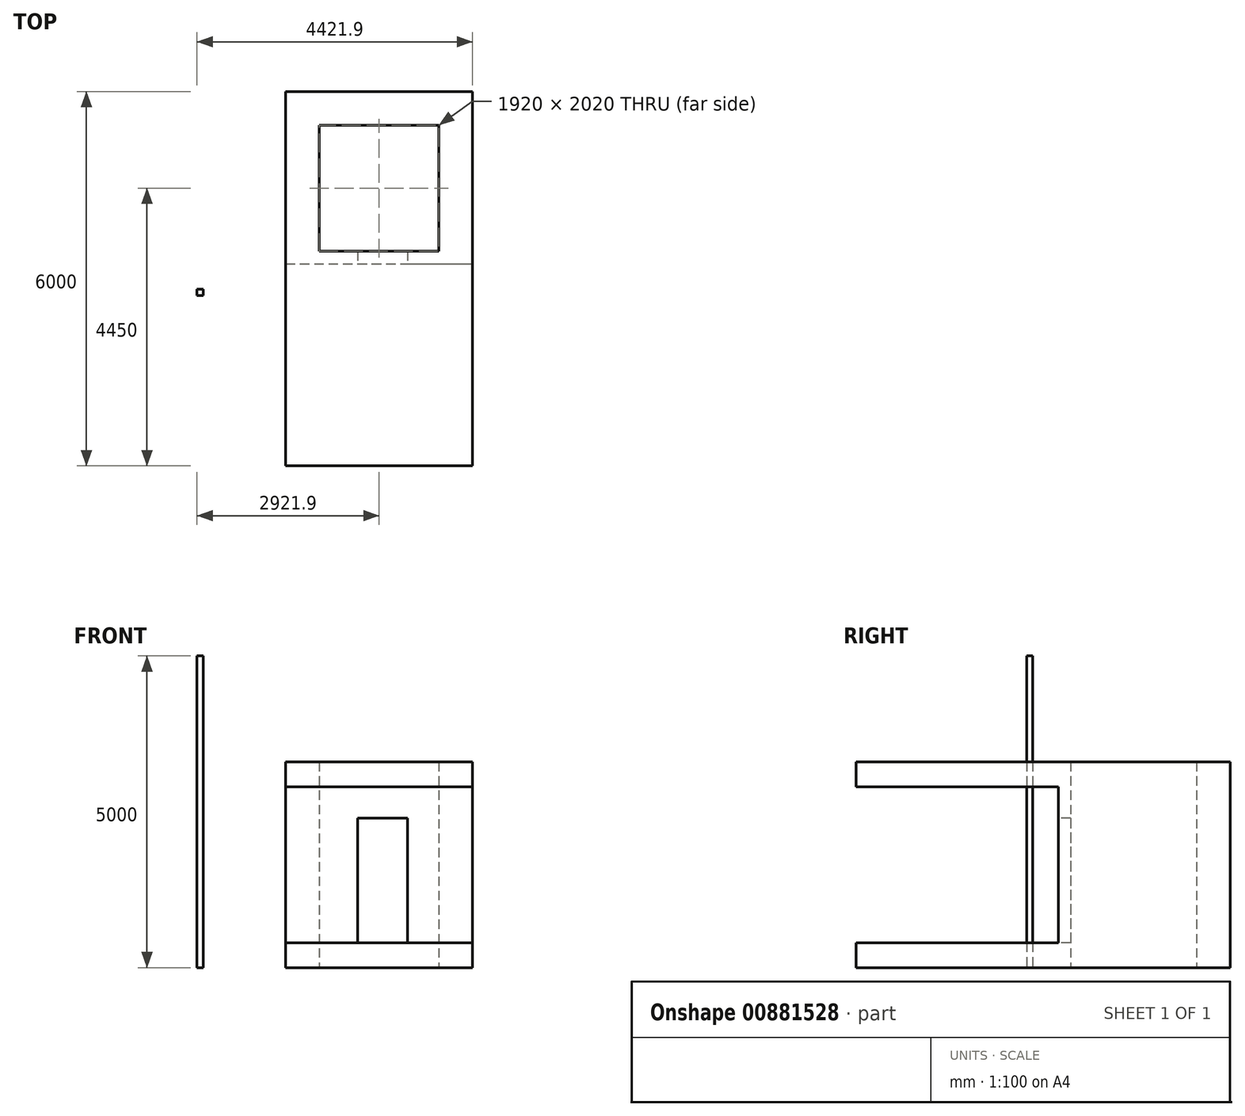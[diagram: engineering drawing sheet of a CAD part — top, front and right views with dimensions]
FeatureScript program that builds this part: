
annotation { "Feature Type Name" : "Feature", "Feature Type Description" : "" }
export const myFeature = defineFeature(function(context is Context, id is Id, definition is map)
    precondition{}
    {
        {
            var Q0;
            Q0=qCreatedBy(makeId("Top.planeOp"),FACE);
            var sketch = newSketch(context, id + "F0", { "sketchPlane" : qUnion([Q0])});
            skLineSegment(sketch, "E0.bottom", {"start": v(-1497.46, 4552.93) * mm, "end": v(1502.54, 4552.93) * mm});
            skLineSegment(sketch, "E0.top", {"start": v(-1497.46, -1447.07) * mm, "end": v(1502.54, -1447.07) * mm});
            skLineSegment(sketch, "E0.left", {"start": v(-1497.46, 4552.93) * mm, "end": v(-1497.46, -1447.07) * mm});
            skLineSegment(sketch, "E0.right", {"start": v(1502.54, 4552.93) * mm, "end": v(1502.54, -1447.07) * mm});
            skLineSegment(sketch, "E1.bottom", {"start": v(-957.46, 4012.93) * mm, "end": v(962.54, 4012.93) * mm});
            skLineSegment(sketch, "E1.top", {"start": v(-957.46, 1992.93) * mm, "end": v(962.54, 1992.93) * mm});
            skLineSegment(sketch, "E1.left", {"start": v(-957.46, 4012.93) * mm, "end": v(-957.46, 1992.93) * mm});
            skLineSegment(sketch, "E1.right", {"start": v(962.54, 4012.93) * mm, "end": v(962.54, 1992.93) * mm});
            skSolve(sketch);
        }
        {
            var Q0;
            Q0=makeQuery(id+"F0.imprint","IMPRINT",FACE,{"disambiguationData":[TD([[makeQuery(id+"F0.imprint","IMPRINT",EDGE,{"derivedFrom":sQuery(id+"F0.wireOp",EDGE,"E0.bottom")}),-1.0]])]});
            extrude(context, id + "F1", {"entities" : qUnion([Q0]), "depth" : 400 * mm, "offsetDistance" : 25 * mm});
        }
        {
            var Q0;
            Q0=makeQuery(id+"F1.opExtrude","CAP_FACE",FACE,{"disambiguationData":[OSD([sQuery(id+"F0.wireOp",EDGE,"E0.bottom"),sQuery(id+"F0.wireOp",EDGE,"E0.top"),sQuery(id+"F0.wireOp",EDGE,"E0.left"),sQuery(id+"F0.wireOp",EDGE,"E0.right"),sQuery(id+"F0.wireOp",EDGE,"E1.bottom"),sQuery(id+"F0.wireOp",EDGE,"E1.top"),sQuery(id+"F0.wireOp",EDGE,"E1.left"),sQuery(id+"F0.wireOp",EDGE,"E1.right")])],"isStart":false});
            var sketch = newSketch(context, id + "F2", { "sketchPlane" : qUnion([Q0])});
            skLineSegment(sketch, "E2.0", {"start": v(-1497.46, 4552.93) * mm, "end": v(1502.54, 4552.93) * mm});
            skLineSegment(sketch, "E3", {"start": v(-1497.46, 1792.93) * mm, "end": v(-342.46, 1792.93) * mm});
            skLineSegment(sketch, "E4", {"start": v(-1497.46, 4552.93) * mm, "end": v(-1497.46, 1792.93) * mm});
            skLineSegment(sketch, "E5", {"start": v(-342.46, 1992.93) * mm, "end": v(-342.46, 1792.93) * mm});
            skLineSegment(sketch, "E6", {"start": v(457.54, 1992.93) * mm, "end": v(457.54, 1792.93) * mm});
            skLineSegment(sketch, "E7.trimOffspring", {"start": v(457.54, 1792.93) * mm, "end": v(1502.54, 1792.93) * mm});
            skLineSegment(sketch, "E8", {"start": v(-342.46, 1992.93) * mm, "end": v(-957.46, 1992.93) * mm});
            skLineSegment(sketch, "E9", {"start": v(-957.46, 1992.93) * mm, "end": v(-957.46, 4012.93) * mm});
            skLineSegment(sketch, "E10", {"start": v(-957.46, 4012.93) * mm, "end": v(962.54, 4012.93) * mm});
            skLineSegment(sketch, "E11", {"start": v(962.54, 4012.93) * mm, "end": v(962.54, 1992.93) * mm});
            skLineSegment(sketch, "E12", {"start": v(962.54, 1992.93) * mm, "end": v(457.54, 1992.93) * mm});
            skLineSegment(sketch, "E13", {"start": v(1502.54, 4552.93) * mm, "end": v(1502.54, 1792.93) * mm});
            skSolve(sketch);
        }
        {
            var Q0;
            Q0 = qSketchRegion(id + "F2", true);
            extrude(context, id + "F3", {"entities" : qUnion([Q0]), "operationType" : NewBodyOperationType.ADD, "depth" : 2000 * mm, "offsetDistance" : 25 * mm});
        }
        {
            var Q0;
            Q0=makeQuery(id+"F3.opExtrude","CAP_FACE",FACE,{"disambiguationData":[OSD([sQuery(id+"F2.wireOp",EDGE,"E2.0"),sQuery(id+"F2.wireOp",EDGE,"E3"),sQuery(id+"F2.wireOp",EDGE,"E4"),sQuery(id+"F2.wireOp",EDGE,"E5"),sQuery(id+"F2.wireOp",EDGE,"E6"),sQuery(id+"F2.wireOp",EDGE,"E7.trimOffspring"),sQuery(id+"F2.wireOp",EDGE,"E8"),sQuery(id+"F2.wireOp",EDGE,"E9"),sQuery(id+"F2.wireOp",EDGE,"E10"),sQuery(id+"F2.wireOp",EDGE,"E11"),sQuery(id+"F2.wireOp",EDGE,"E12"),sQuery(id+"F2.wireOp",EDGE,"E13")])],"isStart":false});
            var sketch = newSketch(context, id + "F4", { "sketchPlane" : qUnion([Q0])});
            skLineSegment(sketch, "E14.bottom", {"start": v(-1497.46, 4552.93) * mm, "end": v(1502.54, 4552.93) * mm});
            skLineSegment(sketch, "E14.top", {"start": v(-1497.46, 1792.93) * mm, "end": v(1502.54, 1792.93) * mm});
            skLineSegment(sketch, "E14.left", {"start": v(-1497.46, 4552.93) * mm, "end": v(-1497.46, 1792.93) * mm});
            skLineSegment(sketch, "E14.right", {"start": v(1502.54, 4552.93) * mm, "end": v(1502.54, 1792.93) * mm});
            skLineSegment(sketch, "E15.bottom", {"start": v(962.54, 1992.93) * mm, "end": v(-957.46, 1992.93) * mm});
            skLineSegment(sketch, "E15.top", {"start": v(962.54, 4012.93) * mm, "end": v(-957.46, 4012.93) * mm});
            skLineSegment(sketch, "E15.left", {"start": v(962.54, 1992.93) * mm, "end": v(962.54, 4012.93) * mm});
            skLineSegment(sketch, "E15.right", {"start": v(-957.46, 1992.93) * mm, "end": v(-957.46, 4012.93) * mm});
            skSolve(sketch);
        }
        {
            var Q0;
            Q0 = qSketchRegion(id + "F4", true);
            extrude(context, id + "F5", {"entities" : qUnion([Q0]), "operationType" : NewBodyOperationType.ADD, "depth" : 500 * mm, "offsetDistance" : 25 * mm});
        }
        {
            var Q0;
            Q0=makeQuery(id+"F5.opExtrude","CAP_FACE",FACE,{"disambiguationData":[OSD([sQuery(id+"F4.wireOp",EDGE,"E14.bottom"),sQuery(id+"F4.wireOp",EDGE,"E14.top"),sQuery(id+"F4.wireOp",EDGE,"E14.left"),sQuery(id+"F4.wireOp",EDGE,"E14.right"),sQuery(id+"F4.wireOp",EDGE,"E15.bottom"),sQuery(id+"F4.wireOp",EDGE,"E15.top"),sQuery(id+"F4.wireOp",EDGE,"E15.left"),sQuery(id+"F4.wireOp",EDGE,"E15.right")])],"isStart":false});
            var sketch = newSketch(context, id + "F6", { "sketchPlane" : qUnion([Q0])});
            skLineSegment(sketch, "E16.0", {"start": v(-1497.46, 4552.93) * mm, "end": v(-1497.46, 1792.93) * mm});
            skLineSegment(sketch, "E17.0", {"start": v(-1497.46, 1792.93) * mm, "end": v(-1497.46, -1447.07) * mm});
            skLineSegment(sketch, "E18.0", {"start": v(-1497.46, -1447.07) * mm, "end": v(1502.54, -1447.07) * mm});
            skLineSegment(sketch, "E19.0", {"start": v(1502.54, 1792.93) * mm, "end": v(1502.54, -1447.07) * mm});
            skLineSegment(sketch, "E20.0", {"start": v(1502.54, 4552.93) * mm, "end": v(1502.54, 1792.93) * mm});
            skLineSegment(sketch, "E21.0", {"start": v(-1497.46, 4552.93) * mm, "end": v(1502.54, 4552.93) * mm});
            skLineSegment(sketch, "E22.0", {"start": v(-957.46, 4012.93) * mm, "end": v(-957.46, 1992.93) * mm});
            skLineSegment(sketch, "E23.0", {"start": v(-957.46, 4012.93) * mm, "end": v(962.54, 4012.93) * mm});
            skLineSegment(sketch, "E24.0", {"start": v(962.54, 4012.93) * mm, "end": v(962.54, 1992.93) * mm});
            skLineSegment(sketch, "E25.0", {"start": v(-957.46, 1992.93) * mm, "end": v(962.54, 1992.93) * mm});
            skSolve(sketch);
        }
        {
            var Q0;
            Q0 = qSketchRegion(id + "F6", true);
            extrude(context, id + "F7", {"entities" : qUnion([Q0]), "operationType" : NewBodyOperationType.ADD, "depth" : 400 * mm, "offsetDistance" : 25 * mm});
        }
        {
            var Q0;
            Q0=qCreatedBy(makeId("Top.planeOp"),FACE);
            var sketch = newSketch(context, id + "F8", { "sketchPlane" : qUnion([Q0])});
            skLineSegment(sketch, "E26.bottom", {"start": v(-2919.36, 1385.46) * mm, "end": v(-2819.36, 1385.46) * mm});
            skLineSegment(sketch, "E26.top", {"start": v(-2919.36, 1285.46) * mm, "end": v(-2819.36, 1285.46) * mm});
            skLineSegment(sketch, "E26.left", {"start": v(-2919.36, 1385.46) * mm, "end": v(-2919.36, 1285.46) * mm});
            skLineSegment(sketch, "E26.right", {"start": v(-2819.36, 1385.46) * mm, "end": v(-2819.36, 1285.46) * mm});
            skSolve(sketch);
        }
        {
            var Q0;
            Q0 = qSketchRegion(id + "F8", true);
            extrude(context, id + "F9", {"entities" : qUnion([Q0]), "depth" : 5000 * mm, "offsetDistance" : 25 * mm});
        }
    });
